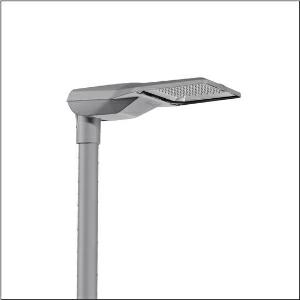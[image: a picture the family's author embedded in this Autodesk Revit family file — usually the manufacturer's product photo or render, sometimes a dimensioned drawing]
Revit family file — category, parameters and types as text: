
# Revit family: streetlight_sl_21_midi___st1_0a_5xe7d23a08lb_9bc0
name_source: partatom
category: Lighting Fixtures
units: mm (PartAtom-declared; Revit-internal decimal feet)

## family parameters
Cut with Voids When Loaded = No
Host = Face
Light Source = No
Part Type = Normal
Room Calculation Point = No
Round Connector Dimension = Use Diameter
Shared = No

## types (1)
- --- (1 x LED, 11880 lm, 98.3 W, 2200K)
    Apparent Load = 98 VA
    CIE Flux Codes = 37 72 97 100 100
    Color Rendering = 70
    Color Temperature = 2200K
    Default Elevation = 1800 mm
    Description = Streetlight SL 21 midi, mast luminaire, primary light control with lens, of PMMA, primary optical cover: cover, of toughened safety glass, transparent, light distribution: ST1.0a, light emission: direct distribution, primary light characteristic: asymmetric, installation type: post-top, side-entry, LED, 3G 1.5mm², High Power LED, rated luminous flux: 11.880lm, luminous efficacy: 121lm/W, light colour: 722, colour temperature: 2200K, control: overheat protection, constant luminous flux control, time-dependent luminous flux control, flexible luminous flux parameterisation, mains connection: 220..240V, AC, 50/60Hz, connection cable pre-assembled, cable length: 10,5m, wiring characteristics: H07RN-F, start of lifetime: 98W, end of service life: 101W, reduction: 44W, luminaire housing, of diecast aluminium, powder-coated, Siteco® metallic grey (DB 702S), corrosivity category C5 mid according to DIN EN ISO 12944, please order mast flange separately, inclination adjustable: 0°, 5°, 10°, 15°, sealing non-destructively replaceable, multi-level sealing system, length: 644mm, width: 335mm, height: 110mm, mast flange for spigot size: 42mm (side-entry): 5XC10008XM4, 60/48mm (side-entry/post-top): 5XC10108XM2, 76/60mm (side-entry/post-top): 5XC10108XM1, protection rating (complete): IP66, insulation class (complete): insulation class II (safety insulation), certification: CE, ENEC, ENEC+, VDE, impact resistance: IK09, permissible operating ambient temperature for outdoor applications: -40..+50°C, standard-compliant lighting for roads and squares, packaging unit: 1 piece

Light Distribution: ST1.0a
    Height = 111 mm
    Lamp = 1 x LED
    Lamp Light Flux = 11880 lm
    Lamp Power = 98.3 W
    Lamp count = 1
    Length = 644 mm
    Luminous efficacy = 121 lm/W
    Manufacturer = Siteco
    ModVariant = No
    Model = 5XE7D23A08LB
    Number of Poles = 1
    OnlyDefault = Yes
    Power Factor = 1
    Product Name = Streetlight SL 21 midi | ST1.0a
    Product group = mast luminaire | pylon top
    ProductGroupID = 6100
    Protection Class = Protection class II
    Protection Degree = IP 66
    RLX_Detail_Level = 1
    RLX_Emergency_Light_Flux = 0 lm
    RLX_Emergency_Type = 0
    RLX_Emergency_Type_DB = No
    RlxData = <blob elided: 90485 chars, md5=19a18890>
    Socket = socket
    Standby Power = 0 W
    System Light Flux = 11880 lm
    System Power = 98 W
    Type Comments = factory setting: luminous flux: 100 % | Output Level: 100 % | 1020 mA
    Type Image = l_1004298.jpg
    URL = http://relux.com
    VarID = @adj_141247
    Voltage = 0 V
    Weight = 0.00 kg
    Width = 336 mm

## geometry (parser evidence)
native form markers: Blend x4, Sweep x14
no freeform markers — native parametric forms only
